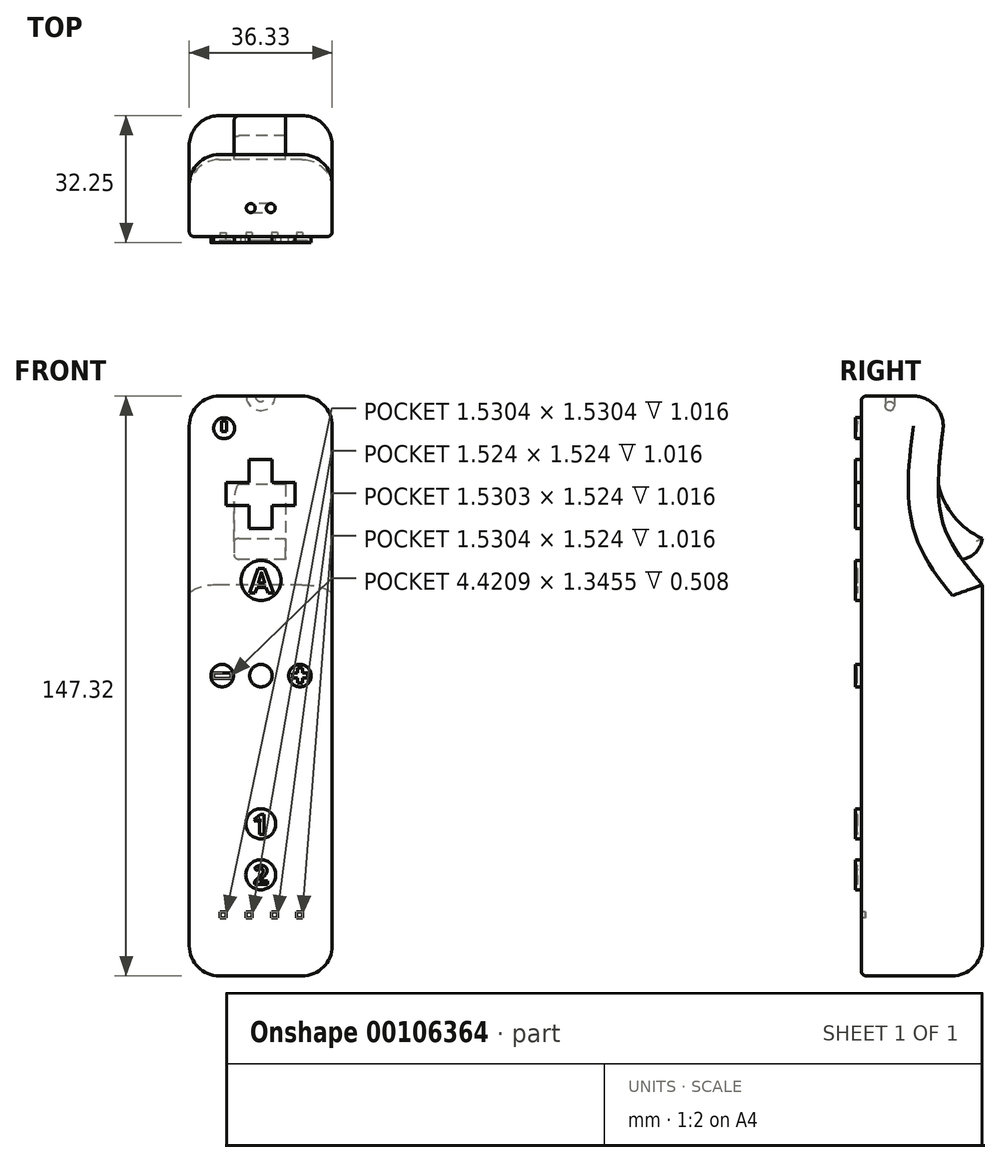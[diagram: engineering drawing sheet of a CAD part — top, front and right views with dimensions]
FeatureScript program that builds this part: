
annotation { "Feature Type Name" : "Feature", "Feature Type Description" : "" }
export const myFeature = defineFeature(function(context is Context, id is Id, definition is map)
    precondition{}
    {
        {
            var Q0;
            Q0=qCreatedBy(makeId("Front.planeOp"),FACE);
            var sketch = newSketch(context, id + "F0", { "sketchPlane" : qUnion([Q0])});
            skLineSegment(sketch, "E0.bottom", {"start": v(16.75, 69.43) * mm, "end": v(53.08, 69.43) * mm});
            skLineSegment(sketch, "E0.top", {"start": v(16.75, -77.89) * mm, "end": v(53.08, -77.89) * mm});
            skLineSegment(sketch, "E0.left", {"start": v(16.75, 69.43) * mm, "end": v(16.75, -77.89) * mm});
            skLineSegment(sketch, "E0.right", {"start": v(53.08, 69.43) * mm, "end": v(53.08, -77.89) * mm});
            skLineSegment(sketch, "E1", {"start": v(16.75, -4.23) * mm, "end": v(53.08, -4.23) * mm, "construction": true});
            skLineSegment(sketch, "E2", {"start": v(16.75, 69.43) * mm, "end": v(16.75, 61.2) * mm, "construction": true});
            skLineSegment(sketch, "E3", {"start": v(34.91, 69.43) * mm, "end": v(34.91, -77.89) * mm, "construction": true});
            skLineSegment(sketch, "E4", {"start": v(16.77, -4.17) * mm, "end": v(53.1, -4.17) * mm, "construction": true});
            skCircle(sketch, "E5", {"center": v(35, 22.59) * mm, "radius": 5.08 * mm});
            skLineSegment(sketch, "E6", {"start": v(31.9, 53.27) * mm, "end": v(37.74, 53.27) * mm});
            skLineSegment(sketch, "E7", {"start": v(37.74, 53.27) * mm, "end": v(37.74, 47.43) * mm});
            skLineSegment(sketch, "E8", {"start": v(37.74, 47.43) * mm, "end": v(43.58, 47.43) * mm});
            skLineSegment(sketch, "E9", {"start": v(43.58, 47.43) * mm, "end": v(43.58, 41.59) * mm});
            skLineSegment(sketch, "E10", {"start": v(43.58, 41.59) * mm, "end": v(37.74, 41.59) * mm});
            skLineSegment(sketch, "E11", {"start": v(37.74, 41.59) * mm, "end": v(37.74, 35.74) * mm});
            skLineSegment(sketch, "E12", {"start": v(37.74, 35.74) * mm, "end": v(31.9, 35.74) * mm});
            skLineSegment(sketch, "E13", {"start": v(31.9, 35.74) * mm, "end": v(31.9, 41.59) * mm});
            skLineSegment(sketch, "E14", {"start": v(31.9, 41.59) * mm, "end": v(26.04, 41.59) * mm});
            skLineSegment(sketch, "E15", {"start": v(26.04, 41.59) * mm, "end": v(26.04, 47.43) * mm});
            skLineSegment(sketch, "E16", {"start": v(26.04, 47.43) * mm, "end": v(31.9, 47.43) * mm});
            skLineSegment(sketch, "E17", {"start": v(31.9, 47.43) * mm, "end": v(31.9, 53.27) * mm});
            skCircle(sketch, "E18", {"center": v(25.62, 61.26) * mm, "radius": 2.66 * mm});
            skPoint(sketch, "E19.startSnap0", {"position": v(34.93, -4.17) * mm});
            skCircle(sketch, "E20", {"center": v(25.11, -1.62) * mm, "radius": 2.86 * mm});
            skCircle(sketch, "E21", {"center": v(34.97, -1.62) * mm, "radius": 2.86 * mm});
            skCircle(sketch, "E22", {"center": v(44.88, -1.62) * mm, "radius": 2.86 * mm});
            skLineSegment(sketch, "E23", {"start": v(34.93, 69.5) * mm, "end": v(34.93, -77.83) * mm, "construction": true});
            skCircle(sketch, "E24", {"center": v(34.93, -52.21) * mm, "radius": 3.81 * mm});
            skCircle(sketch, "E25", {"center": v(34.93, -39.25) * mm, "radius": 3.81 * mm});
            skLineSegment(sketch, "E26.bottom", {"start": v(24.61, -63.16) * mm, "end": v(26.14, -63.16) * mm});
            skLineSegment(sketch, "E26.top", {"start": v(24.61, -61.63) * mm, "end": v(26.14, -61.63) * mm});
            skLineSegment(sketch, "E26.left", {"start": v(24.61, -63.16) * mm, "end": v(24.61, -61.63) * mm});
            skLineSegment(sketch, "E26.right", {"start": v(26.14, -63.16) * mm, "end": v(26.14, -61.63) * mm});
            skLineSegment(sketch, "E27.bottom", {"start": v(32.76, -61.63) * mm, "end": v(31.24, -61.63) * mm});
            skLineSegment(sketch, "E27.top", {"start": v(32.76, -63.16) * mm, "end": v(31.24, -63.16) * mm});
            skLineSegment(sketch, "E27.left", {"start": v(32.76, -61.63) * mm, "end": v(32.76, -63.16) * mm});
            skLineSegment(sketch, "E27.right", {"start": v(31.24, -61.63) * mm, "end": v(31.24, -63.16) * mm});
            skLineSegment(sketch, "E28.bottom", {"start": v(39.14, -61.63) * mm, "end": v(37.6, -61.63) * mm});
            skLineSegment(sketch, "E28.top", {"start": v(39.14, -63.16) * mm, "end": v(37.6, -63.16) * mm});
            skLineSegment(sketch, "E28.left", {"start": v(39.14, -61.63) * mm, "end": v(39.14, -63.16) * mm});
            skLineSegment(sketch, "E28.right", {"start": v(37.6, -61.63) * mm, "end": v(37.6, -63.16) * mm});
            skPoint(sketch, "E29.oppositeSnap0", {"position": v(38.37, -63.16) * mm});
            skLineSegment(sketch, "E29.bottom", {"start": v(45.54, -61.63) * mm, "end": v(44, -61.63) * mm});
            skLineSegment(sketch, "E29.top", {"start": v(45.54, -63.16) * mm, "end": v(44, -63.16) * mm});
            skLineSegment(sketch, "E29.left", {"start": v(45.54, -61.63) * mm, "end": v(45.54, -63.16) * mm});
            skLineSegment(sketch, "E29.right", {"start": v(44, -61.63) * mm, "end": v(44, -63.16) * mm});
            skSolve(sketch);
        }
        {
            var Q0;
            Q0=makeQuery(id+"F0.imprint","IMPRINT",FACE,{"disambiguationData":[TD([[makeQuery(id+"F0.imprint","IMPRINT",EDGE,{"derivedFrom":sQuery(id+"F0.wireOp",EDGE,"E0.bottom")}),-1.0]])]});
            var sketch = newSketch(context, id + "F1", { "sketchPlane" : qUnion([Q0])});
            skLineSegment(sketch, "E30.bottom", {"start": v(16.75, -77.89) * mm, "end": v(53.08, -77.89) * mm});
            skLineSegment(sketch, "E30.top", {"start": v(16.75, 69.43) * mm, "end": v(53.08, 69.43) * mm});
            skLineSegment(sketch, "E30.left", {"start": v(16.75, -77.89) * mm, "end": v(16.75, 69.43) * mm});
            skLineSegment(sketch, "E30.right", {"start": v(53.08, -77.89) * mm, "end": v(53.08, 69.43) * mm});
            skSolve(sketch);
        }
        {
            var Q0;
            Q0=qSketchRegion(id+"F1",true);
            extrude(context, id + "F2", {"entities" : qUnion([Q0]), "oppositeDirection" : true, "depth" : 30.73 * mm});
        }
        {
            var Q0;
            Q0=makeQuery(id+"F2.opExtrude","SWEPT_FACE",FACE,{"disambiguationData":[OSD([sQuery(id+"F1.wireOp",EDGE,"E30.left")])]});
            var sketch = newSketch(context, id + "F3", { "sketchPlane" : qUnion([Q0])});
            skLineSegment(sketch, "E31", {"start": v(-15.37, 69.43) * mm, "end": v(-15.37, -77.89) * mm, "construction": true});
            skFitSpline(sketch, "E32.MirrorCS", {"points": [v(-21.98, 69.43) * mm, v(-19.68, 43.14) * mm, v(-23.3, 31.48) * mm, v(-30.73, 21.46) * mm], "startDerivative": vector(10.07, -68.56) * mm, "endDerivative": vector(-28.1, -34.04) * mm});
            skSolve(sketch);
        }
        {
            var Q0;
            {var subQ0=sQuery(id+"F3.wireOp",EDGE,"E32.MirrorCS");Q0=makeQuery(id+"F3.imprint","IMPRINT",FACE,{"disambiguationData":[TD([[makeQuery(id+"F3.imprint","IMPRINT",EDGE,{"derivedFrom":subQ0}),-1.0]])]});}
            extrude(context, id + "F4", {"entities" : qUnion([Q0]), "operationType" : NewBodyOperationType.REMOVE, "oppositeDirection" : true, "depth" : 37.6 * mm});
        }
        {
            var Q0;
            Q0=makeQuery(id+"F2.opExtrude","SWEPT_EDGE",EDGE,{"disambiguationData":[OSD([sQuery(id+"F1.wireOp",EDGE,"E30.bottom"),sQuery(id+"F1.wireOp",EDGE,"E30.left")])]});
            var Q1;
            Q1=makeQuery(id+"F2.opExtrude","SWEPT_EDGE",EDGE,{"disambiguationData":[OSD([sQuery(id+"F1.wireOp",EDGE,"E30.bottom"),sQuery(id+"F1.wireOp",EDGE,"E30.right")])]});
            var Q2;
            Q2=makeQuery(id+"F2.opExtrude","SWEPT_EDGE",EDGE,{"disambiguationData":[OSD([sQuery(id+"F1.wireOp",EDGE,"E30.top"),sQuery(id+"F1.wireOp",EDGE,"E30.right")])]});
            var Q3;
            Q3=makeQuery(id+"F2.opExtrude","SWEPT_EDGE",EDGE,{"disambiguationData":[OSD([sQuery(id+"F1.wireOp",EDGE,"E30.top"),sQuery(id+"F1.wireOp",EDGE,"E30.left")])]});
            fillet(context, id + "F5", {"entities" : qUnion([Q0, Q1, Q2, Q3]), "radius" : 7.62 * mm, "tangentPropagation" : true, "allowEdgeOverflow" : false});
        }
        {
            var Q0;
            Q0=makeQuery(id+"F2.opExtrude","CAP_EDGE",EDGE,{"disambiguationData":[OSD([sQuery(id+"F1.wireOp",EDGE,"E30.left")])],"isStart":false});
            var Q1;
            Q1=makeQuery(id+"F4.boolean.opBoolean","INTERSECT",EDGE,{"derivedFrom":[makeQuery(id+"F2.opExtrude","SWEPT_FACE",FACE,{"disambiguationData":[OSD([sQuery(id+"F1.wireOp",EDGE,"E30.right")])]}),makeQuery(id+"F4.opExtrude","SWEPT_FACE",FACE,{"disambiguationData":[OSD([sQuery(id+"F3.wireOp",EDGE,"E32.MirrorCS")])]})]});
            var Q2;
            Q2=makeQuery(id+"F4.boolean.opBoolean","COPY",EDGE,{"derivedFrom":makeQuery(id+"F4.opExtrude","SWEPT_EDGE",EDGE,{"disambiguationData":[OSD([sQuery(id+"F1.wireOp",EDGE,"E30.left"),sQuery(id+"F3.wireOp",EDGE,"E32.MirrorCS")])]})});
            fillet(context, id + "F6", {"entities" : qUnion([Q0, Q1, Q2]), "radius" : 7.62 * mm, "tangentPropagation" : true, "allowEdgeOverflow" : false});
        }
        {
            var Q0;
            Q0=makeQuery(id+"F2.opExtrude","CAP_FACE",FACE,{"disambiguationData":[OSD([sQuery(id+"F1.wireOp",EDGE,"E30.bottom"),sQuery(id+"F1.wireOp",EDGE,"E30.top"),sQuery(id+"F1.wireOp",EDGE,"E30.left"),sQuery(id+"F1.wireOp",EDGE,"E30.right")])],"isStart":false});
            var sketch = newSketch(context, id + "F7", { "sketchPlane" : qUnion([Q0])});
            skLineSegment(sketch, "E33", {"start": v(-40.46, 46.91) * mm, "end": v(-29, 46.91) * mm});
            skLineSegment(sketch, "E34", {"start": v(-40.04, 27.96) * mm, "end": v(-29.37, 27.96) * mm});
            skLineSegment(sketch, "E35", {"start": v(-29.37, 27.96) * mm, "end": v(-28.13, 27.96) * mm});
            skLineSegment(sketch, "E36", {"start": v(-40.04, 27.96) * mm, "end": v(-41.28, 27.96) * mm});
            skLineSegment(sketch, "E37", {"start": v(-41.28, 27.96) * mm, "end": v(-41.28, 47.56) * mm});
            skLineSegment(sketch, "E38", {"start": v(-28.13, 27.96) * mm, "end": v(-28.13, 47.72) * mm});
            skLineSegment(sketch, "E39", {"start": v(-40.46, 46.91) * mm, "end": v(-41.28, 46.91) * mm});
            skLineSegment(sketch, "E40", {"start": v(-29, 46.91) * mm, "end": v(-28.13, 46.91) * mm});
            skSolve(sketch);
        }
        {
            var Q0;
            {var subQ4=sQuery(id+"F7.wireOp",EDGE,"E33");Q0=makeQuery(id+"F7.imprint","IMPRINT",FACE,{"disambiguationData":[TD([[makeQuery(id+"F7.imprint","IMPRINT",EDGE,{"derivedFrom":subQ4}),-1.0]])]});}
            var Q1;
            {var subQ0=sQuery(id+"F7.wireOp",EDGE,"K0iS9Brb-cHPL-CKC8-FlRW-324IReGAGtPr");Q1=makeQuery(id+"F7.imprint","IMPRINT",FACE,{"disambiguationData":[TD([[makeQuery(id+"F7.imprint","IMPRINT",EDGE,{"derivedFrom":subQ0}),-1.0]])]});}
            var Q2;
            {var subQ0=sQuery(id+"F7.wireOp",EDGE,"2nC9m2D6-XAsA-QYTj-u19b-e1dphaC4PzCX");Q2=makeQuery(id+"F7.imprint","IMPRINT",FACE,{"disambiguationData":[TD([[makeQuery(id+"F7.imprint","IMPRINT",EDGE,{"derivedFrom":subQ0}),1.0]])]});}
            extrude(context, id + "F8", {"entities" : qUnion([Q0, Q1, Q2]), "operationType" : NewBodyOperationType.ADD, "oppositeDirection" : true, "depth" : 12.7 * mm});
        }
        {
            var Q0;
            Q0=makeQuery(id+"F8.opExtrude","SWEPT_FACE",FACE,{"disambiguationData":[OSD([sQuery(id+"F7.wireOp",EDGE,"E37")])]});
            var sketch = newSketch(context, id + "F9", { "sketchPlane" : qUnion([Q0])});
            skArc(sketch, "E41", {"start": v(19.57, 46.91) * mm, "mid": v(23.59, 38.8) * mm, "end": v(30.73, 33.22) * mm});
            skArc(sketch, "E42", {"start": v(25.6, 27.96) * mm, "mid": v(29.07, 29.72) * mm, "end": v(30.73, 33.22) * mm});
            skSolve(sketch);
        }
        {
            var Q0;
            {var subQ0=sQuery(id+"F9.wireOp",EDGE,"E41");Q0=makeQuery(id+"F9.imprint","IMPRINT",FACE,{"disambiguationData":[TD([[makeQuery(id+"F9.imprint","IMPRINT",EDGE,{"derivedFrom":subQ0}),1.0]])]});}
            var Q1;
            {var subQ0=sQuery(id+"F9.wireOp",EDGE,"oilb41jp-Mc1F-x8EU-rBpX-l4kon2PeC7sV");Q1=makeQuery(id+"F9.imprint","IMPRINT",FACE,{"disambiguationData":[TD([[makeQuery(id+"F9.imprint","IMPRINT",EDGE,{"derivedFrom":subQ0}),-1.0]])]});}
            var Q2;
            {var subQ0=sQuery(id+"F9.wireOp",EDGE,"E42");Q2=makeQuery(id+"F9.imprint","IMPRINT",FACE,{"disambiguationData":[TD([[makeQuery(id+"F9.imprint","IMPRINT",EDGE,{"derivedFrom":subQ0}),-1.0]])]});}
            extrude(context, id + "F10", {"entities" : qUnion([Q0, Q1, Q2]), "operationType" : NewBodyOperationType.REMOVE, "oppositeDirection" : true, "depth" : 15.24 * mm});
        }
        {
            var Q0;
            Q0=makeQuery(id+"F0.imprint","IMPRINT",FACE,{"disambiguationData":[TD([[makeQuery(id+"F0.imprint","IMPRINT",EDGE,{"derivedFrom":sQuery(id+"F0.wireOp",EDGE,"E6")}),-1.0]])]});
            var Q1;
            Q1=makeQuery(id+"F0.imprint","IMPRINT",FACE,{"disambiguationData":[TD([[makeQuery(id+"F0.imprint","IMPRINT",EDGE,{"derivedFrom":sQuery(id+"F0.wireOp",EDGE,"E18")}),1.0]])]});
            var Q2;
            Q2=makeQuery(id+"F0.imprint","IMPRINT",FACE,{"disambiguationData":[TD([[makeQuery(id+"F0.imprint","IMPRINT",EDGE,{"derivedFrom":sQuery(id+"F0.wireOp",EDGE,"E5")}),1.0]])]});
            var Q3;
            Q3=makeQuery(id+"F0.imprint","IMPRINT",FACE,{"disambiguationData":[TD([[makeQuery(id+"F0.imprint","IMPRINT",EDGE,{"derivedFrom":sQuery(id+"F0.wireOp",EDGE,"E21")}),1.0]])]});
            var Q4;
            Q4=makeQuery(id+"F0.imprint","IMPRINT",FACE,{"disambiguationData":[TD([[makeQuery(id+"F0.imprint","IMPRINT",EDGE,{"derivedFrom":sQuery(id+"F0.wireOp",EDGE,"E20")}),1.0]])]});
            var Q5;
            Q5=makeQuery(id+"F0.imprint","IMPRINT",FACE,{"disambiguationData":[TD([[makeQuery(id+"F0.imprint","IMPRINT",EDGE,{"derivedFrom":sQuery(id+"F0.wireOp",EDGE,"E22")}),1.0]])]});
            var Q6;
            Q6=makeQuery(id+"F0.imprint","IMPRINT",FACE,{"disambiguationData":[TD([[makeQuery(id+"F0.imprint","IMPRINT",EDGE,{"derivedFrom":sQuery(id+"F0.wireOp",EDGE,"E25")}),1.0]])]});
            var Q7;
            Q7=makeQuery(id+"F0.imprint","IMPRINT",FACE,{"disambiguationData":[TD([[makeQuery(id+"F0.imprint","IMPRINT",EDGE,{"derivedFrom":sQuery(id+"F0.wireOp",EDGE,"E24")}),1.0]])]});
            extrude(context, id + "F11", {"entities" : qUnion([Q0, Q1, Q2, Q3, Q4, Q5, Q6, Q7]), "operationType" : NewBodyOperationType.ADD, "depth" : 1.52 * mm});
        }
        {
            var Q0;
            Q0=makeQuery(id+"F0.imprint","IMPRINT",FACE,{"disambiguationData":[TD([[makeQuery(id+"F0.imprint","IMPRINT",EDGE,{"derivedFrom":sQuery(id+"F0.wireOp",EDGE,"E29.bottom")}),1.0]])]});
            var Q1;
            Q1=makeQuery(id+"F0.imprint","IMPRINT",FACE,{"disambiguationData":[TD([[makeQuery(id+"F0.imprint","IMPRINT",EDGE,{"derivedFrom":sQuery(id+"F0.wireOp",EDGE,"E28.bottom")}),1.0]])]});
            var Q2;
            Q2=makeQuery(id+"F0.imprint","IMPRINT",FACE,{"disambiguationData":[TD([[makeQuery(id+"F0.imprint","IMPRINT",EDGE,{"derivedFrom":sQuery(id+"F0.wireOp",EDGE,"E27.bottom")}),1.0]])]});
            var Q3;
            Q3=makeQuery(id+"F0.imprint","IMPRINT",FACE,{"disambiguationData":[TD([[makeQuery(id+"F0.imprint","IMPRINT",EDGE,{"derivedFrom":sQuery(id+"F0.wireOp",EDGE,"E26.bottom")}),1.0]])]});
            extrude(context, id + "F12", {"entities" : qUnion([Q0, Q1, Q2, Q3]), "operationType" : NewBodyOperationType.REMOVE, "oppositeDirection" : true, "depth" : 1.02 * mm});
        }
        {
            var Q0;
            Q0=makeQuery(id+"F2.opExtrude","CAP_EDGE",EDGE,{"disambiguationData":[OSD([sQuery(id+"F1.wireOp",EDGE,"E30.left")])],"isStart":true});
            fillet(context, id + "F13", {"entities" : qUnion([Q0]), "radius" : 1.27 * mm, "tangentPropagation" : true, "allowEdgeOverflow" : false});
        }
        {
            var Q0;
            {var subQ0=sQuery(id+"F9.wireOp",EDGE,"E42");var subQ1=sQuery(id+"F7.wireOp",EDGE,"E37");var subQ2=sQuery(id+"F9.wireOp",EDGE,"E41");Q0=makeQuery(id+"F10.boolean.opBoolean","TWEAK_EDGE",EDGE,{"derivedFrom":[makeQuery(id+"F10.opExtrude","SWEPT_EDGE",EDGE,{"disambiguationData":[OSD([subQ1,subQ2,subQ0]),ownerDisambiguation([makeQuery(id+"F10.opExtrude","SWEPT_BODY",BODY,{"disambiguationData":[OSD([subQ1,sQuery(id+"F7.wireOp",EDGE,"E39"),subQ2])]})])]}),makeQuery(id+"F10.opExtrude","SWEPT_EDGE",EDGE,{"disambiguationData":[OSD([subQ1,subQ2,subQ0]),ownerDisambiguation([makeQuery(id+"F10.opExtrude","SWEPT_BODY",BODY,{"disambiguationData":[OSD([sQuery(id+"F7.wireOp",EDGE,"E36"),subQ1,subQ0])]})])]})]});}
            var Q1;
            Q1=makeQuery(id+"F10.boolean.opBoolean","COPY",EDGE,{"derivedFrom":makeQuery(id+"F10.opExtrude","CAP_EDGE",EDGE,{"disambiguationData":[OSD([sQuery(id+"F9.wireOp",EDGE,"E41")])],"isStart":true})});
            var Q2;
            Q2=makeQuery(id+"F10.boolean.opBoolean","INTERSECT",EDGE,{"derivedFrom":[makeQuery(id+"F8.opExtrude","SWEPT_FACE",FACE,{"disambiguationData":[OSD([sQuery(id+"F7.wireOp",EDGE,"E38")])]}),makeQuery(id+"F10.opExtrude","SWEPT_FACE",FACE,{"disambiguationData":[OSD([sQuery(id+"F9.wireOp",EDGE,"E41")])]})]});
            var Q3;
            Q3=makeQuery(id+"F10.boolean.opBoolean","COPY",EDGE,{"derivedFrom":makeQuery(id+"F10.opExtrude","CAP_EDGE",EDGE,{"disambiguationData":[OSD([sQuery(id+"F9.wireOp",EDGE,"E42")])],"isStart":true})});
            var Q4;
            Q4=makeQuery(id+"F10.boolean.opBoolean","INTERSECT",EDGE,{"derivedFrom":[makeQuery(id+"F8.opExtrude","SWEPT_FACE",FACE,{"disambiguationData":[OSD([sQuery(id+"F7.wireOp",EDGE,"E38")])]}),makeQuery(id+"F10.opExtrude","SWEPT_FACE",FACE,{"disambiguationData":[OSD([sQuery(id+"F9.wireOp",EDGE,"E42")])]})]});
            fillet(context, id + "F14", {"entities" : qUnion([Q0, Q1, Q2, Q3, Q4]), "radius" : 1.27 * mm, "tangentPropagation" : true, "allowEdgeOverflow" : false});
        }
        {
            var Q0;
            Q0=makeQuery(id+"F2.opExtrude","SWEPT_FACE",FACE,{"disambiguationData":[OSD([sQuery(id+"F1.wireOp",EDGE,"E30.top")])]});
            var sketch = newSketch(context, id + "F15", { "sketchPlane" : qUnion([Q0])});
            skLineSegment(sketch, "E43", {"start": v(34.91, 13.2) * mm, "end": v(34.91, 1.27) * mm});
            skLineSegment(sketch, "E44", {"start": v(24.37, 7.24) * mm, "end": v(45.46, 7.24) * mm, "construction": true});
            skCircle(sketch, "E45", {"center": v(32.37, 7.24) * mm, "radius": 1.14 * mm});
            skCircle(sketch, "E46", {"center": v(37.45, 7.24) * mm, "radius": 1.14 * mm});
            skLineSegment(sketch, "E47", {"start": v(37.45, 7.24) * mm, "end": v(32.37, 7.24) * mm, "construction": true});
            skSolve(sketch);
        }
        {
            var Q0;
            Q0=makeQuery(id+"F15.imprint","IMPRINT",FACE,{"disambiguationData":[TD([[makeQuery(id+"F15.imprint","IMPRINT",EDGE,{"derivedFrom":sQuery(id+"F15.wireOp",EDGE,"E46")}),1.0]])]});
            var Q1;
            Q1=sQuery(id+"F15.wireOp",EDGE,"E43");
            revolve(context, id + "F16", {"operationType" : NewBodyOperationType.REMOVE, "entities" : qUnion([Q0]), "axis" : qUnion([Q1]), "revolveType" : RevolveType.ONE_DIRECTION, "oppositeDirection" : true, "angle" : 180 * degree});
        }
        {
            var Q0;
            Q0=makeQuery(id+"F11.opExtrude","CAP_FACE",FACE,{"disambiguationData":[OSD([sQuery(id+"F0.wireOp",EDGE,"E5")])],"isStart":false});
            var sketch = newSketch(context, id + "F17", { "sketchPlane" : qUnion([Q0])});
            skText(sketch, "E48", { "text": "A", "fontName": "OpenSans-Bold.ttf"});
            skLineSegment(sketch, "E49.bottom", {"start": v(27.35, -2.32) * mm, "end": v(22.92, -2.32) * mm});
            skLineSegment(sketch, "E49.top", {"start": v(27.35, -0.98) * mm, "end": v(22.92, -0.98) * mm});
            skLineSegment(sketch, "E49.left", {"start": v(27.35, -2.32) * mm, "end": v(27.35, -0.98) * mm});
            skLineSegment(sketch, "E49.right", {"start": v(22.92, -2.32) * mm, "end": v(22.92, -0.98) * mm});
            skPoint(sketch, "E49.middle", {"position": v(25.13, -1.65) * mm});
            skLineSegment(sketch, "E50.bottom", {"start": v(45.51, -3.48) * mm, "end": v(44.24, -3.48) * mm});
            skLineSegment(sketch, "E50.top", {"start": v(45.51, 0.33) * mm, "end": v(44.24, 0.33) * mm});
            skLineSegment(sketch, "E50.left", {"start": v(45.51, -3.48) * mm, "end": v(45.51, -2.21) * mm});
            skLineSegment(sketch, "E50.right", {"start": v(44.24, -3.48) * mm, "end": v(44.24, -2.21) * mm});
            skPoint(sketch, "E50.middle", {"position": v(44.88, -1.57) * mm});
            skLineSegment(sketch, "E51.bottom", {"start": v(46.78, -2.21) * mm, "end": v(45.51, -2.21) * mm});
            skLineSegment(sketch, "E51.top", {"start": v(46.78, -0.93) * mm, "end": v(45.51, -0.93) * mm});
            skLineSegment(sketch, "E51.left", {"start": v(46.78, -2.21) * mm, "end": v(46.78, -0.93) * mm});
            skLineSegment(sketch, "E51.right", {"start": v(42.97, -2.21) * mm, "end": v(42.97, -0.93) * mm});
            skLineSegment(sketch, "E52.trimOffspring", {"start": v(44.24, -0.93) * mm, "end": v(42.97, -0.93) * mm});
            skLineSegment(sketch, "E53.trimOffspring", {"start": v(44.24, -0.93) * mm, "end": v(44.24, 0.33) * mm});
            skLineSegment(sketch, "E54.trimOffspring", {"start": v(45.51, -0.93) * mm, "end": v(45.51, 0.33) * mm});
            skLineSegment(sketch, "E55.trimOffspring", {"start": v(44.24, -2.21) * mm, "end": v(42.97, -2.21) * mm});
            skText(sketch, "E56", { "text": "1", "fontName": "OpenSans-Bold.ttf"});
            skText(sketch, "E57", { "text": "2\n", "fontName": "OpenSans-Bold.ttf"});
            skLineSegment(sketch, "E58.bottom", {"start": v(26.28, 60.43) * mm, "end": v(25, 60.43) * mm});
            skLineSegment(sketch, "E58.left", {"start": v(26.28, 60.43) * mm, "end": v(26.28, 62.34) * mm});
            skLineSegment(sketch, "E58.right", {"start": v(25, 60.43) * mm, "end": v(25, 62.34) * mm});
            skPoint(sketch, "E58.middle", {"position": v(25.64, 61.38) * mm});
            skArc(sketch, "E59", {"start": v(27.16, 61.38) * mm, "mid": v(25.64, 59.86) * mm, "end": v(24.12, 61.38) * mm});
            skArc(sketch, "E60", {"start": v(27.16, 63) * mm, "mid": v(25.64, 59.16) * mm, "end": v(24.12, 63) * mm});
            skArc(sketch, "E61", {"start": v(27.16, 61.38) * mm, "mid": v(25.14, 59.95) * mm, "end": v(24.46, 62.34) * mm});
            skArc(sketch, "E62", {"start": v(27.16, 61.38) * mm, "mid": v(27.08, 61.9) * mm, "end": v(26.82, 62.34) * mm});
            skLineSegment(sketch, "E63", {"start": v(24.46, 62.34) * mm, "end": v(24.12, 63) * mm});
            skLineSegment(sketch, "E64", {"start": v(27.16, 63) * mm, "end": v(26.82, 62.34) * mm});
            skLineSegment(sketch, "E65", {"start": v(25, 62.34) * mm, "end": v(25, 63.1) * mm});
            skLineSegment(sketch, "E66", {"start": v(25, 63.1) * mm, "end": v(26.27, 63.1) * mm});
            skLineSegment(sketch, "E67", {"start": v(26.27, 63.1) * mm, "end": v(26.28, 62.34) * mm});
            const initialGuessF17  = {"E48": [0.03207, 0.01935, 1, 0, 0.00635], "E56": [0.03281, -0.0419, 1, 0, 0.00513], "E57": [0.0331, -0.05461, 1, 0, 0.00476]};
            skSetInitialGuess(sketch, initialGuessF17);
            skSolve(sketch);
        }
        {
            var Q0;
            Q0=makeQuery(id+"F17.imprint","IMPRINT",FACE,{"disambiguationData":[TD([[makeQuery(id+"F17.imprint","IMPRINT",EDGE,{"derivedFrom":sQuery(id+"F17.wireOp",EDGE,"E60")}),-1.0]])]});
            var Q1;
            Q1=makeQuery(id+"F17.imprint","IMPRINT",FACE,{"disambiguationData":[TD([[makeQuery(id+"F17.imprint","IMPRINT",EDGE,{"derivedFrom":sQuery(id+"F17.wireOp",EDGE,"E56.sketch_text.stroke-0")}),-1.0]])]});
            var Q2;
            Q2=makeQuery(id+"F17.imprint","IMPRINT",FACE,{"disambiguationData":[TD([[makeQuery(id+"F17.imprint","IMPRINT",EDGE,{"derivedFrom":sQuery(id+"F17.wireOp",EDGE,"E57.sketch_text.stroke-0")}),-1.0]])]});
            var Q3;
            Q3=makeQuery(id+"F17.imprint","IMPRINT",FACE,{"disambiguationData":[TD([[makeQuery(id+"F17.imprint","IMPRINT",EDGE,{"derivedFrom":sQuery(id+"F17.wireOp",EDGE,"E49.bottom")}),-1.0]])]});
            var Q4;
            Q4=makeQuery(id+"F17.imprint","IMPRINT",FACE,{"disambiguationData":[TD([[makeQuery(id+"F17.imprint","IMPRINT",EDGE,{"derivedFrom":sQuery(id+"F17.wireOp",EDGE,"E50.bottom")}),-1.0]])]});
            var Q5;
            Q5=makeQuery(id+"F17.imprint","IMPRINT",FACE,{"disambiguationData":[TD([[makeQuery(id+"F17.imprint","IMPRINT",EDGE,{"derivedFrom":sQuery(id+"F17.wireOp",EDGE,"E58.bottom")}),-1.0]])]});
            extrude(context, id + "F18", {"entities" : qUnion([Q0, Q1, Q2, Q3, Q4, Q5]), "operationType" : NewBodyOperationType.REMOVE, "oppositeDirection" : true, "depth" : 0.5 * mm});
        }
        {
            var Q0;
            Q0=makeQuery(id+"F17.imprint","IMPRINT",FACE,{"disambiguationData":[TD([[makeQuery(id+"F17.imprint","IMPRINT",EDGE,{"derivedFrom":sQuery(id+"F17.wireOp",EDGE,"E48.sketch_text.stroke-0")}),-1.0]])]});
            extrude(context, id + "F19", {"entities" : qUnion([Q0]), "operationType" : NewBodyOperationType.REMOVE, "oppositeDirection" : true, "depth" : 0.5 * mm});
        }
    });
